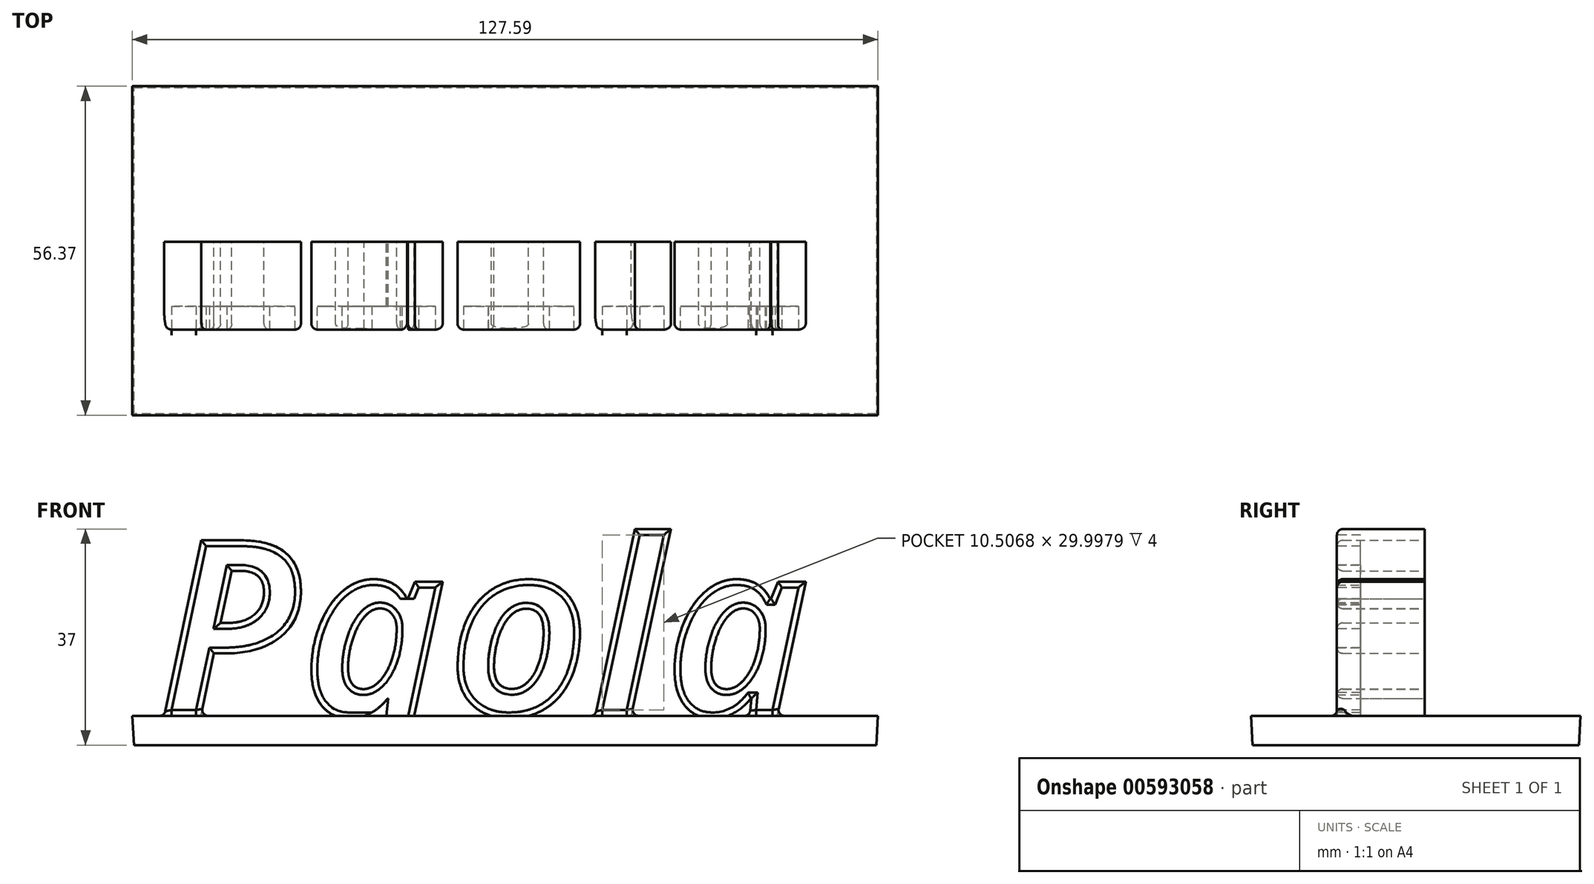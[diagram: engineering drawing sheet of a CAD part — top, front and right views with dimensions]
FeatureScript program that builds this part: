
annotation { "Feature Type Name" : "Feature", "Feature Type Description" : "" }
export const myFeature = defineFeature(function(context is Context, id is Id, definition is map)
    precondition{}
    {
        {
            var Q0;
            Q0=qCreatedBy(makeId("Top.planeOp"),FACE);
            var sketch = newSketch(context, id + "F0", { "sketchPlane" : qUnion([Q0])});
            skLineSegment(sketch, "E0.bottom", {"start": v(-60.91, 26.43) * mm, "end": v(66.16, 26.43) * mm});
            skLineSegment(sketch, "E0.top", {"start": v(-60.91, -29.42) * mm, "end": v(66.16, -29.42) * mm});
            skLineSegment(sketch, "E0.left", {"start": v(-60.91, 26.43) * mm, "end": v(-60.91, -29.42) * mm});
            skLineSegment(sketch, "E0.right", {"start": v(66.16, 26.43) * mm, "end": v(66.16, -29.42) * mm});
            skSolve(sketch);
        }
        {
            var Q0;
            Q0=makeQuery(id+"F0.imprint","IMPRINT",FACE,{"disambiguationData":[TD([[makeQuery(id+"F0.imprint","IMPRINT",EDGE,{"derivedFrom":sQuery(id+"F0.wireOp",EDGE,"E0.bottom")}),-1.0]])]});
            extrude(context, id + "F1", {"entities" : qUnion([Q0]), "depth" : 5 * mm, "offsetDistance" : 25 * mm, "hasDraft" : true, "draftAngle" : 3 * degree});
        }
        {
            var Q0;
            Q0=qCreatedBy(makeId("Front.planeOp"),FACE);
            var sketch = newSketch(context, id + "F2", { "sketchPlane" : qUnion([Q0])});
            skText(sketch, "E1", { "text": "Paola", "fontName": "OpenSans-BoldItalic.ttf"});
            const initialGuessF2  = {"E1": [-0.0568, 0.005, 1, 0, 0.03032]};
            skSetInitialGuess(sketch, initialGuessF2);
            skSolve(sketch);
        }
        {
            var Q0;
            Q0 = qSketchRegion(id + "F2", true);
            extrude(context, id + "F3", {"entities" : qUnion([Q0]), "operationType" : NewBodyOperationType.ADD, "depth" : 15 * mm, "offsetDistance" : 25 * mm});
        }
        {
            var Q0;
            Q0=makeQuery(id+"F3.opExtrude","CAP_FACE",FACE,{"disambiguationData":[OSD([sQuery(id+"F2.wireOp",EDGE,"E1.sketch_text.stroke-51"),sQuery(id+"F2.wireOp",EDGE,"E1.sketch_text.stroke-52"),sQuery(id+"F2.wireOp",EDGE,"E1.sketch_text.stroke-53"),sQuery(id+"F2.wireOp",EDGE,"E1.sketch_text.stroke-54"),sQuery(id+"F2.wireOp",EDGE,"E1.sketch_text.stroke-55"),sQuery(id+"F2.wireOp",EDGE,"E1.sketch_text.stroke-56"),sQuery(id+"F2.wireOp",EDGE,"E1.sketch_text.stroke-57"),sQuery(id+"F2.wireOp",EDGE,"E1.sketch_text.stroke-58"),sQuery(id+"F2.wireOp",EDGE,"E1.sketch_text.stroke-59"),sQuery(id+"F2.wireOp",EDGE,"E1.sketch_text.stroke-60"),sQuery(id+"F2.wireOp",EDGE,"E1.sketch_text.stroke-61"),sQuery(id+"F2.wireOp",EDGE,"E1.sketch_text.stroke-62"),sQuery(id+"F2.wireOp",EDGE,"E1.sketch_text.stroke-63"),sQuery(id+"F2.wireOp",EDGE,"E1.sketch_text.stroke-64"),sQuery(id+"F2.wireOp",EDGE,"E1.sketch_text.stroke-65"),sQuery(id+"F2.wireOp",EDGE,"E1.sketch_text.stroke-66"),sQuery(id+"F2.wireOp",EDGE,"E1.sketch_text.stroke-67"),sQuery(id+"F2.wireOp",EDGE,"E1.sketch_text.stroke-68"),sQuery(id+"F2.wireOp",EDGE,"E1.sketch_text.stroke-69"),sQuery(id+"F2.wireOp",EDGE,"E1.sketch_text.stroke-70")])],"isStart":false});
            var Q1;
            Q1=makeQuery(id+"F3.opExtrude","CAP_EDGE",EDGE,{"disambiguationData":[OSD([sQuery(id+"F2.wireOp",EDGE,"E1.sketch_text.stroke-65")])],"isStart":false});
            fillet(context, id + "F4", {"entities" : qUnion([Q0, Q1]), "radius" : 1 * mm, "tangentPropagation" : true, "allowEdgeOverflow" : false});
        }
        {
            var Q0;
            Q0=makeQuery(id+"F3.opExtrude","CAP_FACE",FACE,{"disambiguationData":[OSD([sQuery(id+"F2.wireOp",EDGE,"E1.sketch_text.stroke-71"),sQuery(id+"F2.wireOp",EDGE,"E1.sketch_text.stroke-72"),sQuery(id+"F2.wireOp",EDGE,"E1.sketch_text.stroke-73"),sQuery(id+"F2.wireOp",EDGE,"E1.sketch_text.stroke-74")])],"isStart":false});
            fillet(context, id + "F5", {"entities" : qUnion([Q0]), "radius" : 1 * mm, "tangentPropagation" : true, "allowEdgeOverflow" : false});
        }
        {
            var Q0;
            Q0=makeQuery(id+"F3.opExtrude","CAP_FACE",FACE,{"disambiguationData":[OSD([sQuery(id+"F2.wireOp",EDGE,"E1.sketch_text.stroke-0"),sQuery(id+"F2.wireOp",EDGE,"E1.sketch_text.stroke-1"),sQuery(id+"F2.wireOp",EDGE,"E1.sketch_text.stroke-2"),sQuery(id+"F2.wireOp",EDGE,"E1.sketch_text.stroke-3"),sQuery(id+"F2.wireOp",EDGE,"E1.sketch_text.stroke-4"),sQuery(id+"F2.wireOp",EDGE,"E1.sketch_text.stroke-5"),sQuery(id+"F2.wireOp",EDGE,"E1.sketch_text.stroke-6"),sQuery(id+"F2.wireOp",EDGE,"E1.sketch_text.stroke-7"),sQuery(id+"F2.wireOp",EDGE,"E1.sketch_text.stroke-8"),sQuery(id+"F2.wireOp",EDGE,"E1.sketch_text.stroke-9"),sQuery(id+"F2.wireOp",EDGE,"E1.sketch_text.stroke-10"),sQuery(id+"F2.wireOp",EDGE,"E1.sketch_text.stroke-11"),sQuery(id+"F2.wireOp",EDGE,"E1.sketch_text.stroke-12"),sQuery(id+"F2.wireOp",EDGE,"E1.sketch_text.stroke-13"),sQuery(id+"F2.wireOp",EDGE,"E1.sketch_text.stroke-14"),sQuery(id+"F2.wireOp",EDGE,"E1.sketch_text.stroke-15"),sQuery(id+"F2.wireOp",EDGE,"E1.sketch_text.stroke-16"),sQuery(id+"F2.wireOp",EDGE,"E1.sketch_text.stroke-17"),sQuery(id+"F2.wireOp",EDGE,"E1.sketch_text.stroke-18"),sQuery(id+"F2.wireOp",EDGE,"E1.sketch_text.stroke-19"),sQuery(id+"F2.wireOp",EDGE,"E1.sketch_text.stroke-20"),sQuery(id+"F2.wireOp",EDGE,"E1.sketch_text.stroke-21"),sQuery(id+"F2.wireOp",EDGE,"E1.sketch_text.stroke-22"),sQuery(id+"F2.wireOp",EDGE,"E1.sketch_text.stroke-23"),sQuery(id+"F2.wireOp",EDGE,"E1.sketch_text.stroke-24"),sQuery(id+"F2.wireOp",EDGE,"E1.sketch_text.stroke-25")])],"isStart":false});
            fillet(context, id + "F6", {"entities" : qUnion([Q0]), "radius" : 1 * mm, "tangentPropagation" : true, "allowEdgeOverflow" : false});
        }
        {
            var Q0;
            Q0=makeQuery(id+"F3.opExtrude","CAP_EDGE",EDGE,{"disambiguationData":[OSD([sQuery(id+"F2.wireOp",EDGE,"E1.sketch_text.stroke-18")])],"isStart":false});
            var Q1;
            Q1=makeQuery(id+"F3.opExtrude","CAP_EDGE",EDGE,{"disambiguationData":[OSD([sQuery(id+"F2.wireOp",EDGE,"E1.sketch_text.stroke-36")])],"isStart":false});
            var Q2;
            Q2=makeQuery(id+"F3.opExtrude","CAP_EDGE",EDGE,{"disambiguationData":[OSD([sQuery(id+"F2.wireOp",EDGE,"E1.sketch_text.stroke-53")])],"isStart":false});
            var Q3;
            Q3=makeQuery(id+"F3.opExtrude","CAP_EDGE",EDGE,{"disambiguationData":[OSD([sQuery(id+"F2.wireOp",EDGE,"E1.sketch_text.stroke-43")])],"isStart":false});
            var Q4;
            Q4=makeQuery(id+"F3.opExtrude","CAP_EDGE",EDGE,{"disambiguationData":[OSD([sQuery(id+"F2.wireOp",EDGE,"E1.sketch_text.stroke-24")])],"isStart":false});
            var Q5;
            Q5=makeQuery(id+"F3.opExtrude","CAP_EDGE",EDGE,{"disambiguationData":[OSD([sQuery(id+"F2.wireOp",EDGE,"E1.sketch_text.stroke-25")])],"isStart":false});
            var Q6;
            Q6=makeQuery(id+"F3.opExtrude","CAP_EDGE",EDGE,{"disambiguationData":[OSD([sQuery(id+"F2.wireOp",EDGE,"E1.sketch_text.stroke-26")])],"isStart":false});
            var Q7;
            Q7=makeQuery(id+"F3.opExtrude","CAP_EDGE",EDGE,{"disambiguationData":[OSD([sQuery(id+"F2.wireOp",EDGE,"E1.sketch_text.stroke-23")])],"isStart":false});
            fillet(context, id + "F7", {"entities" : qUnion([Q0, Q1, Q2, Q3, Q4, Q5, Q6, Q7]), "radius" : 1 * mm, "tangentPropagation" : true, "allowEdgeOverflow" : false});
        }
        {
            var Q0;
            Q0=makeQuery(id+"F3.opExtrude","CAP_FACE",FACE,{"disambiguationData":[OSD([sQuery(id+"F2.wireOp",EDGE,"E1.sketch_text.stroke-0"),sQuery(id+"F2.wireOp",EDGE,"E1.sketch_text.stroke-1"),sQuery(id+"F2.wireOp",EDGE,"E1.sketch_text.stroke-2"),sQuery(id+"F2.wireOp",EDGE,"E1.sketch_text.stroke-3"),sQuery(id+"F2.wireOp",EDGE,"E1.sketch_text.stroke-4"),sQuery(id+"F2.wireOp",EDGE,"E1.sketch_text.stroke-5"),sQuery(id+"F2.wireOp",EDGE,"E1.sketch_text.stroke-6"),sQuery(id+"F2.wireOp",EDGE,"E1.sketch_text.stroke-7"),sQuery(id+"F2.wireOp",EDGE,"E1.sketch_text.stroke-8"),sQuery(id+"F2.wireOp",EDGE,"E1.sketch_text.stroke-9"),sQuery(id+"F2.wireOp",EDGE,"E1.sketch_text.stroke-10"),sQuery(id+"F2.wireOp",EDGE,"E1.sketch_text.stroke-11"),sQuery(id+"F2.wireOp",EDGE,"E1.sketch_text.stroke-12"),sQuery(id+"F2.wireOp",EDGE,"E1.sketch_text.stroke-13"),sQuery(id+"F2.wireOp",EDGE,"E1.sketch_text.stroke-14")])],"isStart":false});
            var Q1;
            Q1=makeQuery(id+"F3.opExtrude","CAP_FACE",FACE,{"disambiguationData":[OSD([sQuery(id+"F2.wireOp",EDGE,"E1.sketch_text.stroke-15"),sQuery(id+"F2.wireOp",EDGE,"E1.sketch_text.stroke-16"),sQuery(id+"F2.wireOp",EDGE,"E1.sketch_text.stroke-17"),sQuery(id+"F2.wireOp",EDGE,"E1.sketch_text.stroke-18"),sQuery(id+"F2.wireOp",EDGE,"E1.sketch_text.stroke-19"),sQuery(id+"F2.wireOp",EDGE,"E1.sketch_text.stroke-20"),sQuery(id+"F2.wireOp",EDGE,"E1.sketch_text.stroke-21"),sQuery(id+"F2.wireOp",EDGE,"E1.sketch_text.stroke-22"),sQuery(id+"F2.wireOp",EDGE,"E1.sketch_text.stroke-23"),sQuery(id+"F2.wireOp",EDGE,"E1.sketch_text.stroke-24"),sQuery(id+"F2.wireOp",EDGE,"E1.sketch_text.stroke-25"),sQuery(id+"F2.wireOp",EDGE,"E1.sketch_text.stroke-26"),sQuery(id+"F2.wireOp",EDGE,"E1.sketch_text.stroke-27"),sQuery(id+"F2.wireOp",EDGE,"E1.sketch_text.stroke-28"),sQuery(id+"F2.wireOp",EDGE,"E1.sketch_text.stroke-29"),sQuery(id+"F2.wireOp",EDGE,"E1.sketch_text.stroke-30"),sQuery(id+"F2.wireOp",EDGE,"E1.sketch_text.stroke-31"),sQuery(id+"F2.wireOp",EDGE,"E1.sketch_text.stroke-32"),sQuery(id+"F2.wireOp",EDGE,"E1.sketch_text.stroke-33"),sQuery(id+"F2.wireOp",EDGE,"E1.sketch_text.stroke-34"),sQuery(id+"F2.wireOp",EDGE,"E1.sketch_text.stroke-35"),sQuery(id+"F2.wireOp",EDGE,"E1.sketch_text.stroke-36"),sQuery(id+"F2.wireOp",EDGE,"E1.sketch_text.stroke-37"),sQuery(id+"F2.wireOp",EDGE,"E1.sketch_text.stroke-38"),sQuery(id+"F2.wireOp",EDGE,"E1.sketch_text.stroke-39")])],"isStart":false});
            var Q2;
            Q2=makeQuery(id+"F3.opExtrude","CAP_FACE",FACE,{"disambiguationData":[OSD([sQuery(id+"F2.wireOp",EDGE,"E1.sketch_text.stroke-40"),sQuery(id+"F2.wireOp",EDGE,"E1.sketch_text.stroke-41"),sQuery(id+"F2.wireOp",EDGE,"E1.sketch_text.stroke-42"),sQuery(id+"F2.wireOp",EDGE,"E1.sketch_text.stroke-43"),sQuery(id+"F2.wireOp",EDGE,"E1.sketch_text.stroke-44"),sQuery(id+"F2.wireOp",EDGE,"E1.sketch_text.stroke-45"),sQuery(id+"F2.wireOp",EDGE,"E1.sketch_text.stroke-46"),sQuery(id+"F2.wireOp",EDGE,"E1.sketch_text.stroke-47"),sQuery(id+"F2.wireOp",EDGE,"E1.sketch_text.stroke-48"),sQuery(id+"F2.wireOp",EDGE,"E1.sketch_text.stroke-49"),sQuery(id+"F2.wireOp",EDGE,"E1.sketch_text.stroke-50"),sQuery(id+"F2.wireOp",EDGE,"E1.sketch_text.stroke-51"),sQuery(id+"F2.wireOp",EDGE,"E1.sketch_text.stroke-52"),sQuery(id+"F2.wireOp",EDGE,"E1.sketch_text.stroke-53"),sQuery(id+"F2.wireOp",EDGE,"E1.sketch_text.stroke-54"),sQuery(id+"F2.wireOp",EDGE,"E1.sketch_text.stroke-55"),sQuery(id+"F2.wireOp",EDGE,"E1.sketch_text.stroke-56"),sQuery(id+"F2.wireOp",EDGE,"E1.sketch_text.stroke-57")])],"isStart":false});
            var Q3;
            Q3=makeQuery(id+"F3.opExtrude","CAP_FACE",FACE,{"disambiguationData":[OSD([sQuery(id+"F2.wireOp",EDGE,"E1.sketch_text.stroke-58"),sQuery(id+"F2.wireOp",EDGE,"E1.sketch_text.stroke-59"),sQuery(id+"F2.wireOp",EDGE,"E1.sketch_text.stroke-60"),sQuery(id+"F2.wireOp",EDGE,"E1.sketch_text.stroke-61")])],"isStart":false});
            var Q4;
            Q4=makeQuery(id+"F3.opExtrude","CAP_FACE",FACE,{"disambiguationData":[OSD([sQuery(id+"F2.wireOp",EDGE,"E1.sketch_text.stroke-62"),sQuery(id+"F2.wireOp",EDGE,"E1.sketch_text.stroke-63"),sQuery(id+"F2.wireOp",EDGE,"E1.sketch_text.stroke-64"),sQuery(id+"F2.wireOp",EDGE,"E1.sketch_text.stroke-65"),sQuery(id+"F2.wireOp",EDGE,"E1.sketch_text.stroke-66"),sQuery(id+"F2.wireOp",EDGE,"E1.sketch_text.stroke-67"),sQuery(id+"F2.wireOp",EDGE,"E1.sketch_text.stroke-68"),sQuery(id+"F2.wireOp",EDGE,"E1.sketch_text.stroke-69"),sQuery(id+"F2.wireOp",EDGE,"E1.sketch_text.stroke-70"),sQuery(id+"F2.wireOp",EDGE,"E1.sketch_text.stroke-71"),sQuery(id+"F2.wireOp",EDGE,"E1.sketch_text.stroke-72"),sQuery(id+"F2.wireOp",EDGE,"E1.sketch_text.stroke-73"),sQuery(id+"F2.wireOp",EDGE,"E1.sketch_text.stroke-74"),sQuery(id+"F2.wireOp",EDGE,"E1.sketch_text.stroke-75"),sQuery(id+"F2.wireOp",EDGE,"E1.sketch_text.stroke-76"),sQuery(id+"F2.wireOp",EDGE,"E1.sketch_text.stroke-77"),sQuery(id+"F2.wireOp",EDGE,"E1.sketch_text.stroke-78"),sQuery(id+"F2.wireOp",EDGE,"E1.sketch_text.stroke-79"),sQuery(id+"F2.wireOp",EDGE,"E1.sketch_text.stroke-80"),sQuery(id+"F2.wireOp",EDGE,"E1.sketch_text.stroke-81"),sQuery(id+"F2.wireOp",EDGE,"E1.sketch_text.stroke-82"),sQuery(id+"F2.wireOp",EDGE,"E1.sketch_text.stroke-83"),sQuery(id+"F2.wireOp",EDGE,"E1.sketch_text.stroke-84"),sQuery(id+"F2.wireOp",EDGE,"E1.sketch_text.stroke-85"),sQuery(id+"F2.wireOp",EDGE,"E1.sketch_text.stroke-86")])],"isStart":false});
            extrude(context, id + "F8", {"entities" : qUnion([Q0, Q1, Q2, Q3, Q4]), "operationType" : NewBodyOperationType.REMOVE, "oppositeDirection" : true, "depth" : 4 * mm, "offsetDistance" : 25 * mm});
        }
    });
